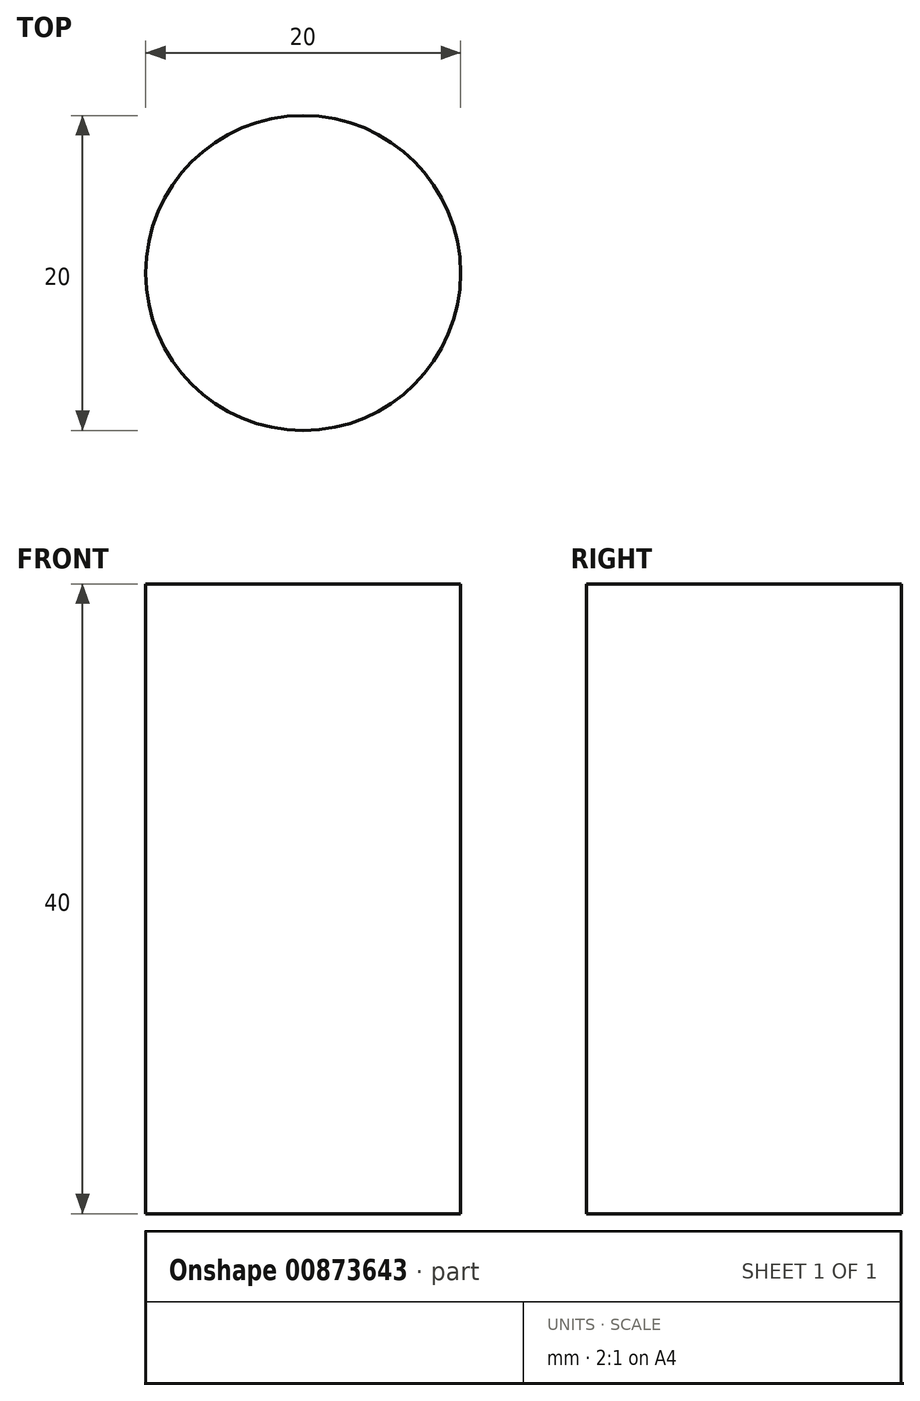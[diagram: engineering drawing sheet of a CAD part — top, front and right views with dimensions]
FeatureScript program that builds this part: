
annotation { "Feature Type Name" : "Feature", "Feature Type Description" : "" }
export const myFeature = defineFeature(function(context is Context, id is Id, definition is map)
    precondition{}
    {
        {
            var Q0;
            Q0=qCreatedBy(makeId("Top.planeOp"),FACE);
            var sketch = newSketch(context, id + "F0", { "sketchPlane" : qUnion([Q0])});
            skCircle(sketch, "E0", {"center": v(0, 0) * mm, "radius": 10 * mm});
            skSolve(sketch);
        }
        {
            var Q0;
            Q0 = qSketchRegion(id + "F0", true);
            extrude(context, id + "F1", {"entities" : qUnion([Q0]), "depth" : 40 * mm, "offsetDistance" : 25 * mm});
        }
    });
